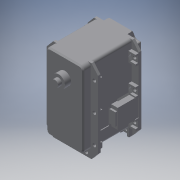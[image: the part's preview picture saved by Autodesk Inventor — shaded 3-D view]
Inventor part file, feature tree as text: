
AUTODESK INVENTOR PART (.ipt)
format: ipt  version: 2016 (Build 200138000, 138)  size: 501,760 bytes
history: native  units: in
note: dims shown in document units (in); Inventor stores cm internally (conversion verified against a paired STEP export)
features: extrude x1, sketch x1, projected_geometry x1, imported_body x1
ambient origin geometry x8: Origin, YZ Plane, XZ Plane, XY Plane, X Axis, Y Axis, Z Axis, Center Point
bodies: Solid1 (feature_tree)
feature tree (4):
  extrude  "Extrusion1"  [1 undecoded]
  sketch  "Sketch1"  dims[d0=0.1181in d1=0.0in]
  projected_geometry  "Projected Loop1"
  imported_body  "Base1"
note: 1 required parameter value undecoded (feature->parameter linkage not recoverable at this tier; creation-order binding heuristic only, values carry confidence <= 0.55)
